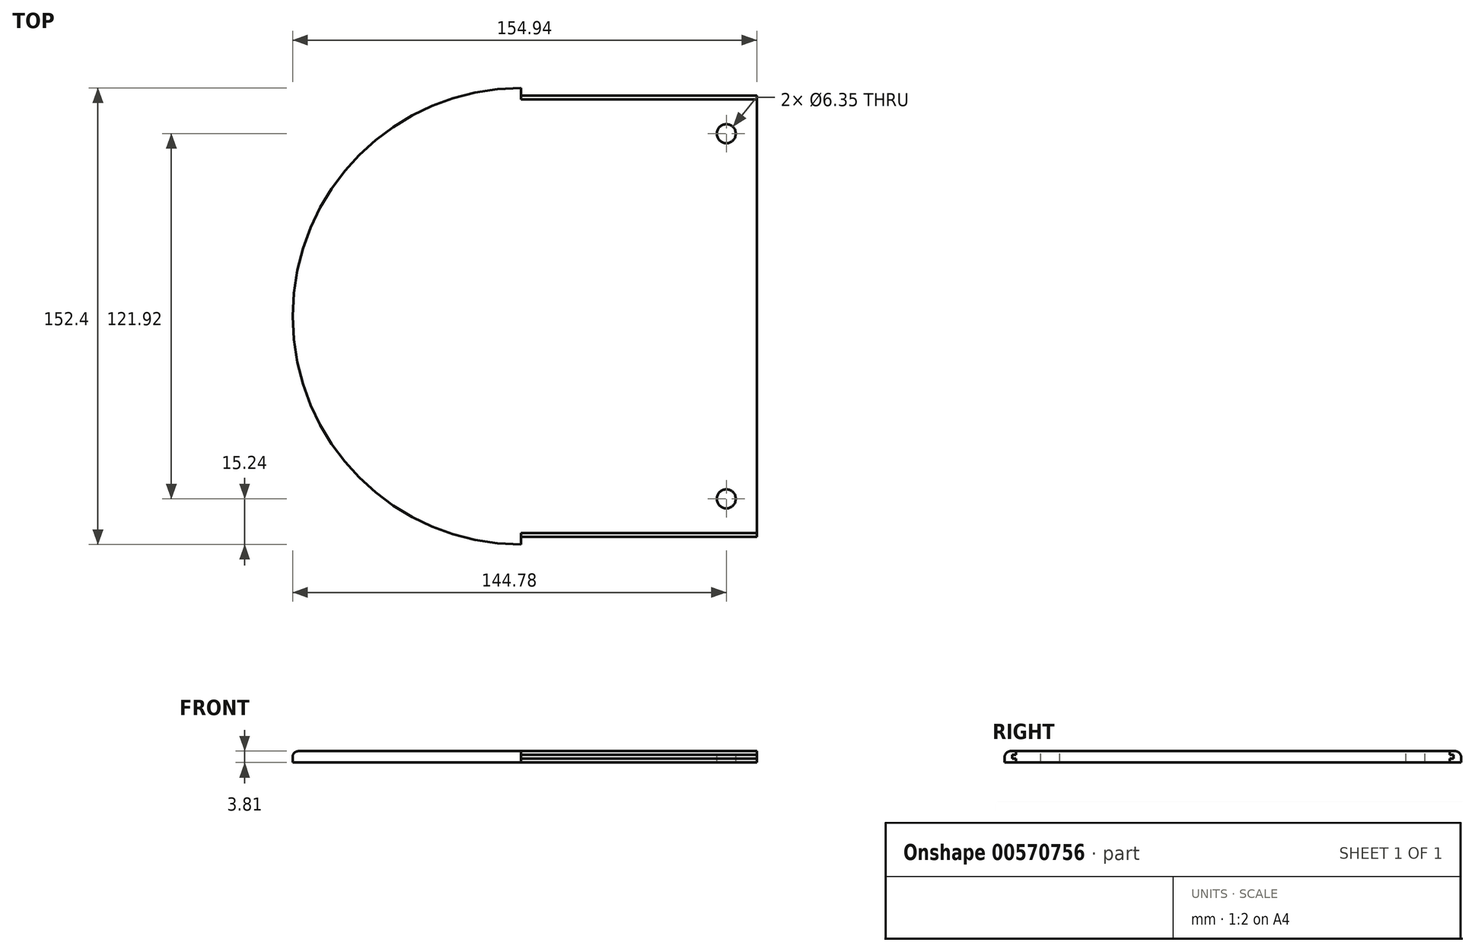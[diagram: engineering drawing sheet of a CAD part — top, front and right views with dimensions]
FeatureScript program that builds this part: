
annotation { "Feature Type Name" : "Feature", "Feature Type Description" : "" }
export const myFeature = defineFeature(function(context is Context, id is Id, definition is map)
    precondition{}
    {
        {
            var Q0;
            Q0=qCreatedBy(makeId("Top.planeOp"),FACE);
            var sketch = newSketch(context, id + "F0", { "sketchPlane" : qUnion([Q0])});
            skCircle(sketch, "E0", {"center": v(0, 0) * mm, "radius": 76.2 * mm});
            skLineSegment(sketch, "E1.bottom", {"start": v(0, 76.2) * mm, "end": v(78.74, 76.2) * mm});
            skLineSegment(sketch, "E1.top", {"start": v(0, -76.2) * mm, "end": v(78.74, -76.2) * mm});
            skLineSegment(sketch, "E1.left", {"start": v(0, 76.2) * mm, "end": v(0, -76.2) * mm});
            skLineSegment(sketch, "E1.right", {"start": v(78.74, 76.2) * mm, "end": v(78.74, -76.2) * mm});
            skSolve(sketch);
        }
        {
            var Q0;
            {var subQ0=sQuery(id+"F0.wireOp",EDGE,"E1.left");Q0=makeQuery(id+"F0.imprint","IMPRINT",FACE,{"disambiguationData":[TD([[makeQuery(id+"F0.imprint","IMPRINT",EDGE,{"derivedFrom":subQ0}),-1.0]])]});}
            var Q1;
            {var subQ0=sQuery(id+"F0.wireOp",EDGE,"E1.left");Q1=makeQuery(id+"F0.imprint","IMPRINT",FACE,{"disambiguationData":[TD([[makeQuery(id+"F0.imprint","IMPRINT",EDGE,{"derivedFrom":subQ0}),1.0]])]});}
            var Q2;
            {var subQ1=sQuery(id+"F0.wireOp",EDGE,"E1.bottom");Q2=makeQuery(id+"F0.imprint","IMPRINT",FACE,{"disambiguationData":[TD([[makeQuery(id+"F0.imprint","IMPRINT",EDGE,{"derivedFrom":subQ1}),-1.0]])]});}
            extrude(context, id + "F1", {"entities" : qUnion([Q0, Q1, Q2]), "depth" : 3.8 * mm, "offsetDistance" : 25.4 * mm});
        }
        {
            var Q0;
            Q0=makeQuery(id+"F1.opExtrude","SWEPT_FACE",FACE,{"disambiguationData":[OSD([sQuery(id+"F0.wireOp",EDGE,"E1.right")])]});
            var sketch = newSketch(context, id + "F2", { "sketchPlane" : qUnion([Q0])});
            skLineSegment(sketch, "E2.bottom", {"start": v(-76.2, 3.81) * mm, "end": v(-73.66, 3.81) * mm});
            skLineSegment(sketch, "E2.top", {"start": v(-76.2, 0) * mm, "end": v(-73.66, 0) * mm});
            skLineSegment(sketch, "E2.left", {"start": v(-76.2, 3.81) * mm, "end": v(-76.2, 0) * mm});
            skLineSegment(sketch, "E2.right", {"start": v(-73.66, 3.81) * mm, "end": v(-73.66, 0) * mm});
            skLineSegment(sketch, "E3", {"start": v(0, 0) * mm, "end": v(0, 3.81) * mm});
            skLineSegment(sketch, "E4.MirrorCS", {"start": v(73.66, 3.81) * mm, "end": v(73.66, 0) * mm});
            skLineSegment(sketch, "E5.MirrorCS", {"start": v(76.2, 3.81) * mm, "end": v(76.2, 0) * mm});
            skLineSegment(sketch, "E6.MirrorCS", {"start": v(76.2, 3.81) * mm, "end": v(73.66, 3.81) * mm});
            skLineSegment(sketch, "E7.MirrorCS", {"start": v(76.2, 0) * mm, "end": v(73.66, 0) * mm});
            skSolve(sketch);
        }
        {
            var Q0;
            Q0=makeQuery(id+"F2.imprint","IMPRINT",FACE,{"disambiguationData":[TD([[makeQuery(id+"F2.imprint","IMPRINT",EDGE,{"derivedFrom":sQuery(id+"F2.wireOp",EDGE,"E2.bottom")}),1.0]])]});
            var Q1;
            Q1=makeQuery(id+"F2.imprint","IMPRINT",FACE,{"disambiguationData":[TD([[makeQuery(id+"F2.imprint","IMPRINT",EDGE,{"derivedFrom":sQuery(id+"F2.wireOp",EDGE,"E4.MirrorCS")}),1.0]])]});
            extrude(context, id + "F3", {"entities" : qUnion([Q0, Q1]), "operationType" : NewBodyOperationType.REMOVE, "oppositeDirection" : true, "depth" : 78.74 * mm, "offsetDistance" : 25.4 * mm});
        }
        {
            var Q0;
            Q0=makeQuery(id+"F1.opExtrude","SWEPT_FACE",FACE,{"disambiguationData":[OSD([sQuery(id+"F0.wireOp",EDGE,"E1.right")])]});
            var sketch = newSketch(context, id + "F4", { "sketchPlane" : qUnion([Q0])});
            skLineSegment(sketch, "E8", {"start": v(-73.66, 1.9) * mm, "end": v(73.66, 1.9) * mm});
            skLineSegment(sketch, "E9", {"start": v(0, 0) * mm, "end": v(0, 3.81) * mm});
            skLineSegment(sketch, "E10.bottom", {"start": v(-73.66, 3.81) * mm, "end": v(-72.4, 3.81) * mm});
            skLineSegment(sketch, "E10.top", {"start": v(-73.66, 2.54) * mm, "end": v(-72.4, 2.54) * mm});
            skLineSegment(sketch, "E10.left", {"start": v(-73.66, 3.81) * mm, "end": v(-73.66, 2.54) * mm});
            skLineSegment(sketch, "E10.right", {"start": v(-72.4, 3.81) * mm, "end": v(-72.4, 2.54) * mm});
            skLineSegment(sketch, "E11.MirrorCS", {"start": v(-73.66, 1.27) * mm, "end": v(-72.4, 1.27) * mm});
            skLineSegment(sketch, "E12.MirrorCS", {"start": v(-72.4, 0) * mm, "end": v(-72.4, 1.27) * mm});
            skLineSegment(sketch, "E13.MirrorCS", {"start": v(-73.66, 0) * mm, "end": v(-73.66, 1.27) * mm});
            skLineSegment(sketch, "E14.MirrorCS", {"start": v(-73.66, 0) * mm, "end": v(-72.4, 0) * mm});
            skLineSegment(sketch, "E15.MirrorCS", {"start": v(72.4, 3.81) * mm, "end": v(72.4, 2.54) * mm});
            skLineSegment(sketch, "E16.MirrorCS", {"start": v(73.66, 2.54) * mm, "end": v(72.4, 2.54) * mm});
            skLineSegment(sketch, "E17.MirrorCS", {"start": v(73.66, 3.81) * mm, "end": v(73.66, 2.54) * mm});
            skLineSegment(sketch, "E18.MirrorCS", {"start": v(73.66, 3.81) * mm, "end": v(72.4, 3.81) * mm});
            skLineSegment(sketch, "E19.MirrorCS", {"start": v(73.66, 1.27) * mm, "end": v(72.4, 1.27) * mm});
            skLineSegment(sketch, "E20.MirrorCS", {"start": v(73.66, 0) * mm, "end": v(73.66, 1.27) * mm});
            skLineSegment(sketch, "E21.MirrorCS", {"start": v(73.66, 0) * mm, "end": v(72.4, 0) * mm});
            skLineSegment(sketch, "E22.MirrorCS", {"start": v(72.4, 0) * mm, "end": v(72.4, 1.27) * mm});
            skSolve(sketch);
        }
        {
            var Q0;
            Q0=makeQuery(id+"F4.imprint","IMPRINT",FACE,{"disambiguationData":[TD([[makeQuery(id+"F4.imprint","IMPRINT",EDGE,{"derivedFrom":sQuery(id+"F4.wireOp",EDGE,"E10.bottom")}),1.0]])]});
            var Q1;
            Q1=makeQuery(id+"F4.imprint","IMPRINT",FACE,{"disambiguationData":[TD([[makeQuery(id+"F4.imprint","IMPRINT",EDGE,{"derivedFrom":sQuery(id+"F4.wireOp",EDGE,"E11.MirrorCS")}),-1.0]])]});
            var Q2;
            Q2=makeQuery(id+"F4.imprint","IMPRINT",FACE,{"disambiguationData":[TD([[makeQuery(id+"F4.imprint","IMPRINT",EDGE,{"derivedFrom":sQuery(id+"F4.wireOp",EDGE,"E15.MirrorCS")}),1.0]])]});
            var Q3;
            Q3=makeQuery(id+"F4.imprint","IMPRINT",FACE,{"disambiguationData":[TD([[makeQuery(id+"F4.imprint","IMPRINT",EDGE,{"derivedFrom":sQuery(id+"F4.wireOp",EDGE,"E19.MirrorCS")}),1.0]])]});
            extrude(context, id + "F5", {"entities" : qUnion([Q0, Q1, Q2, Q3]), "operationType" : NewBodyOperationType.REMOVE, "oppositeDirection" : true, "depth" : 78.74 * mm, "offsetDistance" : 25.4 * mm});
        }
        {
            var Q0;
            Q0=makeQuery(id+"F1.opExtrude","CAP_FACE",FACE,{"disambiguationData":[OSD([sQuery(id+"F0.wireOp",EDGE,"E0"),sQuery(id+"F0.wireOp",EDGE,"E1.bottom"),sQuery(id+"F0.wireOp",EDGE,"E1.top"),sQuery(id+"F0.wireOp",EDGE,"E1.right")])],"isStart":false});
            var sketch = newSketch(context, id + "F6", { "sketchPlane" : qUnion([Q0])});
            skCircle(sketch, "E23", {"center": v(68.58, 60.96) * mm, "radius": 3.18 * mm});
            skCircle(sketch, "E24", {"center": v(68.58, -60.96) * mm, "radius": 3.18 * mm});
            skSolve(sketch);
        }
        {
            var Q0;
            Q0=makeQuery(id+"F6.imprint","IMPRINT",FACE,{"disambiguationData":[TD([[makeQuery(id+"F6.imprint","IMPRINT",EDGE,{"derivedFrom":sQuery(id+"F6.wireOp",EDGE,"E23")}),1.0]])]});
            var Q1;
            Q1=makeQuery(id+"F6.imprint","IMPRINT",FACE,{"disambiguationData":[TD([[makeQuery(id+"F6.imprint","IMPRINT",EDGE,{"derivedFrom":sQuery(id+"F6.wireOp",EDGE,"BoNyElww-dP8s-Om9l-tDQR-4JIRlCJVs43c")}),1.0]])]});
            var Q2;
            Q2=makeQuery(id+"F6.imprint","IMPRINT",FACE,{"disambiguationData":[TD([[makeQuery(id+"F6.imprint","IMPRINT",EDGE,{"derivedFrom":sQuery(id+"F6.wireOp",EDGE,"E24")}),1.0]])]});
            extrude(context, id + "F7", {"entities" : qUnion([Q0, Q1, Q2]), "operationType" : NewBodyOperationType.REMOVE, "oppositeDirection" : true, "depth" : 25.4 * mm, "offsetDistance" : 25.4 * mm});
        }
        {
            var Q0;
            Q0=makeQuery(id+"F1.opExtrude","CAP_EDGE",EDGE,{"disambiguationData":[OSD([sQuery(id+"F0.wireOp",EDGE,"E0")])],"isStart":false});
            fillet(context, id + "F8", {"entities" : qUnion([Q0]), "radius" : 2.03 * mm, "tangentPropagation" : true, "allowEdgeOverflow" : false});
        }
    });
